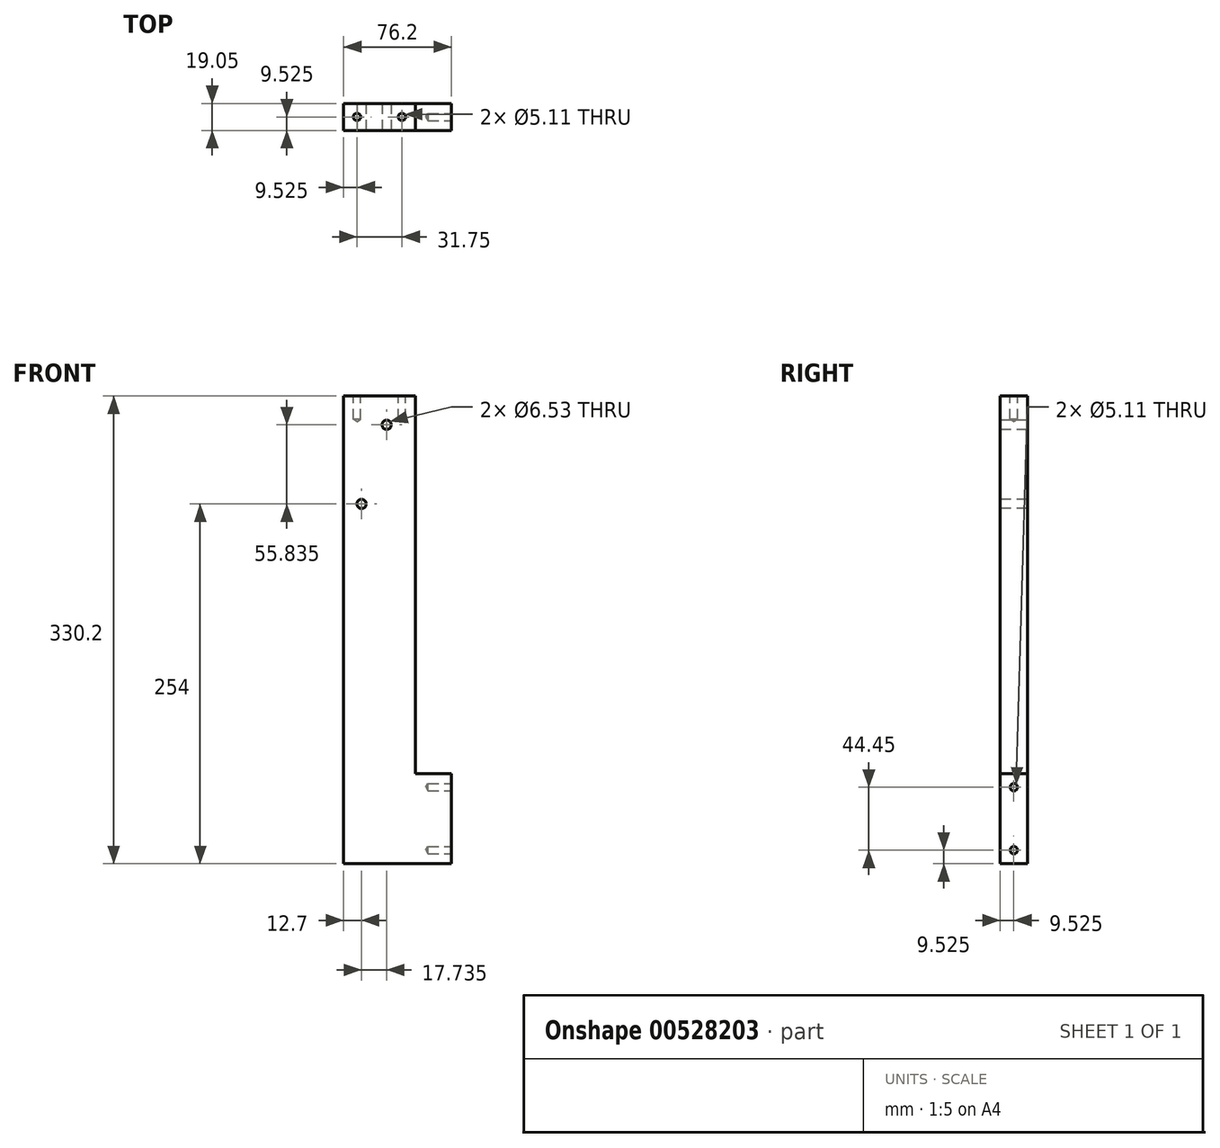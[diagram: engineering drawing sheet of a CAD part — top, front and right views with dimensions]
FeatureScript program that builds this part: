
annotation { "Feature Type Name" : "Feature", "Feature Type Description" : "" }
export const myFeature = defineFeature(function(context is Context, id is Id, definition is map)
    precondition{}
    {
        {
            var Q0;
            Q0=qCreatedBy(makeId("Front.planeOp"),FACE);
            var sketch = newSketch(context, id + "F0", { "sketchPlane" : qUnion([Q0])});
            skLineSegment(sketch, "E0.bottom", {"start": v(0, 0) * mm, "end": v(76.2, 0) * mm});
            skLineSegment(sketch, "E0.top", {"start": v(0, 330.2) * mm, "end": v(76.2, 330.2) * mm});
            skLineSegment(sketch, "E0.left", {"start": v(0, 0) * mm, "end": v(0, 330.2) * mm});
            skLineSegment(sketch, "E0.right", {"start": v(76.2, 0) * mm, "end": v(76.2, 330.2) * mm});
            skSolve(sketch);
        }
        {
            var Q0;
            Q0 = qSketchRegion(id + "F0", true);
            extrude(context, id + "F1", {"entities" : qUnion([Q0]), "depth" : 19.05 * mm, "offsetDistance" : 25.4 * mm});
        }
        {
            var Q0;
            Q0=makeQuery(id+"F0.imprint","IMPRINT",FACE,{"disambiguationData":[TD([[makeQuery(id+"F0.imprint","IMPRINT",EDGE,{"derivedFrom":sQuery(id+"F0.wireOp",EDGE,"E0.bottom")}),1.0]])]});
            var sketch = newSketch(context, id + "F2", { "sketchPlane" : qUnion([Q0])});
            skLineSegment(sketch, "E1.bottom", {"start": v(76.2, 330.2) * mm, "end": v(50.8, 330.2) * mm});
            skLineSegment(sketch, "E1.top", {"start": v(76.2, 63.5) * mm, "end": v(50.8, 63.5) * mm});
            skLineSegment(sketch, "E1.left", {"start": v(76.2, 330.2) * mm, "end": v(76.2, 63.5) * mm});
            skLineSegment(sketch, "E1.right", {"start": v(50.8, 330.2) * mm, "end": v(50.8, 63.5) * mm});
            skSolve(sketch);
        }
        {
            var Q0;
            Q0 = qSketchRegion(id + "F2", true);
            extrude(context, id + "F3", {"entities" : qUnion([Q0]), "operationType" : NewBodyOperationType.REMOVE, "endBound" : BoundingType.THROUGH_ALL, "depth" : 25.4 * mm, "offsetDistance" : 25.4 * mm});
        }
        {
            var Q0;
            Q0=makeQuery(id+"F1.opExtrude","CAP_FACE",FACE,{"disambiguationData":[OSD([sQuery(id+"F0.wireOp",EDGE,"E0.bottom"),sQuery(id+"F0.wireOp",EDGE,"E0.top"),sQuery(id+"F0.wireOp",EDGE,"E0.left"),sQuery(id+"F0.wireOp",EDGE,"E0.right")])],"isStart":false});
            var sketch = newSketch(context, id + "F4", { "sketchPlane" : qUnion([Q0])});
            skCircle(sketch, "E2", {"center": v(12.7, 254) * mm, "radius": 3.26 * mm});
            skSolve(sketch);
        }
        {
            var Q0;
            Q0 = qSketchRegion(id + "F4", true);
            extrude(context, id + "F5", {"entities" : qUnion([Q0]), "operationType" : NewBodyOperationType.REMOVE, "endBound" : BoundingType.THROUGH_ALL, "oppositeDirection" : true, "depth" : 25.4 * mm, "offsetDistance" : 25.4 * mm});
        }
        {
            var Q0;
            Q0=makeQuery(id+"F1.opExtrude","CAP_FACE",FACE,{"disambiguationData":[OSD([sQuery(id+"F0.wireOp",EDGE,"E0.bottom"),sQuery(id+"F0.wireOp",EDGE,"E0.top"),sQuery(id+"F0.wireOp",EDGE,"E0.left"),sQuery(id+"F0.wireOp",EDGE,"E0.right")])],"isStart":false});
            var sketch = newSketch(context, id + "F6", { "sketchPlane" : qUnion([Q0])});
            skCircle(sketch, "E3", {"center": v(30.44, 309.84) * mm, "radius": 20.36 * mm, "construction": true});
            skCircle(sketch, "E4", {"center": v(30.44, 309.84) * mm, "radius": 3.26 * mm});
            skSolve(sketch);
        }
        {
            var Q0;
            Q0=makeQuery(id+"F6.imprint","IMPRINT",FACE,{"disambiguationData":[TD([[makeQuery(id+"F6.imprint","IMPRINT",EDGE,{"derivedFrom":sQuery(id+"F6.wireOp",EDGE,"E4")}),1.0]])]});
            var Q1;
            Q1=sQuery(id+"F6.wireOp",EDGE,"E4");
            extrude(context, id + "F7", {"entities" : qUnion([Q0]), "operationType" : NewBodyOperationType.REMOVE, "surfaceEntities" : qUnion([Q1]), "endBound" : BoundingType.THROUGH_ALL, "oppositeDirection" : true, "depth" : 25.4 * mm, "offsetDistance" : 25.4 * mm});
        }
        {
            var Q0;
            Q0=makeQuery(id+"F1.opExtrude","SWEPT_FACE",FACE,{"disambiguationData":[OSD([sQuery(id+"F0.wireOp",EDGE,"E0.top")])]});
            var sketch = newSketch(context, id + "F8", { "sketchPlane" : qUnion([Q0])});
            skPoint(sketch, "E5", {"position": v(9.53, -9.53) * mm});
            skPoint(sketch, "E6", {"position": v(41.27, -9.53) * mm});
            skLineSegment(sketch, "E7", {"start": v(0, -9.53) * mm, "end": v(50.8, -9.53) * mm, "construction": true});
            skCircle(sketch, "E8", {"center": v(0, -9.53) * mm, "radius": 9.53 * mm, "construction": true});
            skCircle(sketch, "E9", {"center": v(50.8, -9.53) * mm, "radius": 9.53 * mm, "construction": true});
            skSolve(sketch);
        }
        {
            var Q0;
            Q0=sQuery(id+"F8.wireOp",VERTEX,"E5");
            var Q1;
            Q1=sQuery(id+"F8.wireOp",VERTEX,"E6");
            var Q2;
            Q2=makeQuery(id+"F1.opExtrude","SWEPT_BODY",BODY,{"disambiguationData":[OSD([sQuery(id+"F0.wireOp",EDGE,"E0.bottom"),sQuery(id+"F0.wireOp",EDGE,"E0.top"),sQuery(id+"F0.wireOp",EDGE,"E0.left"),sQuery(id+"F0.wireOp",EDGE,"E0.right")])]});
            hole(context, id + "F9", {"style" : HoleStyle.SIMPLE, "endStyle" : HoleEndStyle.BLIND, "standardTappedOrClearance" : lookupTablePath({ "standard" : "ANSI", "engagement" : "75%", "pitch" : "20 tpi", "size" : "1/4", "type" : "Tapped" }), "standardBlindInLast" : lookupTablePath({ "standard" : "ANSI", "engagement" : "75%", "pitch" : "20 tpi", "size" : "1/4", "type" : "Tapped" }), "holeDiameter" : 5.1 * mm, "majorDiameter" : 6.35 * mm, "showTappedDepth" : true, "holeDepth" : 16.51 * mm, "isTappedThrough" : true, "tappedDepth" : 12.7 * mm, "tapClearance" : 3, "startFromSketch" : true, "locations" : qUnion([Q0, Q1]), "scope" : qUnion([Q2])});
        }
        {
            var Q0;
            Q0=makeQuery(id+"F1.opExtrude","SWEPT_FACE",FACE,{"disambiguationData":[OSD([sQuery(id+"F0.wireOp",EDGE,"E0.right")])]});
            var sketch = newSketch(context, id + "F10", { "sketchPlane" : qUnion([Q0])});
            skLineSegment(sketch, "E10", {"start": v(-9.53, 63.5) * mm, "end": v(-9.53, 0) * mm, "construction": true});
            skCircle(sketch, "E11", {"center": v(-9.53, 63.5) * mm, "radius": 9.53 * mm, "construction": true});
            skCircle(sketch, "E12", {"center": v(-9.53, 0) * mm, "radius": 9.53 * mm, "construction": true});
            skPoint(sketch, "E13", {"position": v(-9.53, 53.97) * mm});
            skPoint(sketch, "E14", {"position": v(-9.53, 9.52) * mm});
            skSolve(sketch);
        }
        {
            var Q0;
            Q0=sQuery(id+"F10.wireOp",VERTEX,"E13");
            var Q1;
            Q1=sQuery(id+"F10.wireOp",VERTEX,"E14");
            var Q2;
            Q2=makeQuery(id+"F1.opExtrude","SWEPT_BODY",BODY,{"disambiguationData":[OSD([sQuery(id+"F0.wireOp",EDGE,"E0.bottom"),sQuery(id+"F0.wireOp",EDGE,"E0.top"),sQuery(id+"F0.wireOp",EDGE,"E0.left"),sQuery(id+"F0.wireOp",EDGE,"E0.right")])]});
            hole(context, id + "F11", {"style" : HoleStyle.SIMPLE, "endStyle" : HoleEndStyle.BLIND, "standardTappedOrClearance" : lookupTablePath({ "standard" : "ANSI", "engagement" : "75%", "pitch" : "20 tpi", "size" : "1/4", "type" : "Tapped" }), "standardBlindInLast" : lookupTablePath({ "standard" : "ANSI", "engagement" : "75%", "pitch" : "20 tpi", "size" : "1/4", "type" : "Tapped" }), "holeDiameter" : 5.1 * mm, "majorDiameter" : 6.35 * mm, "showTappedDepth" : true, "holeDepth" : 16.5 * mm, "isTappedThrough" : true, "tappedDepth" : 12.7 * mm, "tapClearance" : 3, "startFromSketch" : true, "locations" : qUnion([Q0, Q1]), "scope" : qUnion([Q2])});
        }
    });
